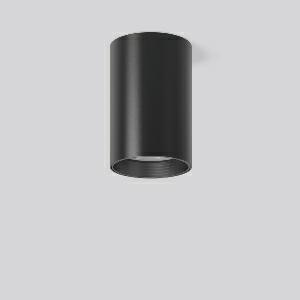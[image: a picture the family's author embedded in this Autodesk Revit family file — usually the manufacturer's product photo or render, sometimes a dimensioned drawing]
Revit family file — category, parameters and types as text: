
# Revit family: heledon_maxi_a_931220_003_2_6198
name_source: partatom
category: Lighting Fixtures
units: mm (PartAtom-declared; Revit-internal decimal feet)

## family parameters
Cut with Voids When Loaded = No
Host = Face
Light Source = No
Part Type = Normal
Room Calculation Point = No
Round Connector Dimension = Use Diameter
Shared = No

## types (1)
- HELEDON maxi A (1 x LED Modul 927, 2650 lm, 2700)
    Apparent Load = 25 VA
    Approval mark = CE
    CIE Flux Codes = 97 100 100 100 100
    Color Rendering = 92
    Color Temperature = 2700
    Default Elevation = 1800 mm
    Description = Series: HELEDON maxi
Cylindrical surface-mounted downlight. Housing: die-cast aluminium, powder-coated. Internal ceiling frame polycarbonate with bayonet mounting. Black plastic ring and recessed LED to prevent glare from the side. Optical assembly with lens made of plastic (polycarbonate) for the best homogeneous light distribution - can be changed without tools. Best colour rendering index Ra>90. Suitable for Ceiling mounting. Easy installation with a separate ceiling frame with bayonet mounting and plug connection. Driver integrated. Connected via plug-in connector. High quality converter without flickering and stroboscopic effect. The following accessories can be mounted without use of tools: interchangeable lenses, decorative glasses, honeycomb louvre, clear and frosted diffusers, white interchangeable plastic ring. 
Colour: deep black, matt (RAL 9005)
Diameter: 123 mm
Height: 183 mm
Lamp: LED
Socket: without socket
Colour temperature: 2700K
Colour rendering index (CRI): 92
System power: 25 W
Rated luminous flux: 2650 lm
Luminous efficiency: 106 lm/W
Control gear: Regulated power supply
Protection class: I
Type of protection: IP 20
    Height = 183 mm
    Lamp = 1 x LED Modul 927
    Lamp Light Flux = 2650 lm
    Lamp count = 1
    Length = 123 mm
    Lifetime = 50000 h
    Luminous efficacy = 106 lm/W
    Manufacturer = RZB
    ModVariant = No
    Model = 931220.003.2
    Mounting Place = Ceiling
    Mounting Type = Surface mounted
    Number of Poles = 1
    OnlyDefault = Yes
    Power Factor = 1
    Product Name = HELEDON maxi A
    Product group = Surface mounted downlights
    ProductGroupID = 302
    Protection Class = Protection class I
    Protection Degree = IP 20
    RLX_Detail_Level = 1
    RLX_Emergency_Light_Flux = 0 lm
    RLX_Emergency_Type = 0
    RLX_Emergency_Type_DB = No
    RlxData = <blob elided: 94605 chars, md5=787cf5da>
    Socket = socket
    Standby Power = 0 W
    System Light Flux = 2650 lm
    System Power = 25 W
    Type Comments = Product without accessories
    Type Image = 931193.003.jpg
    URL = http://relux.com
    VarID = ---
    Voltage = 230 V
    Voltage Range = 220-240 V
    Weight = 0.00 kg
    Width = 0 mm  [stored 0 ft]

note: [stored X ft] marks values corroborated as IEEE doubles in the binary element streams (Revit-internal decimal feet)

## geometry (parser evidence)
native form markers: Blend x4, Sweep x11
no freeform markers — native parametric forms only
